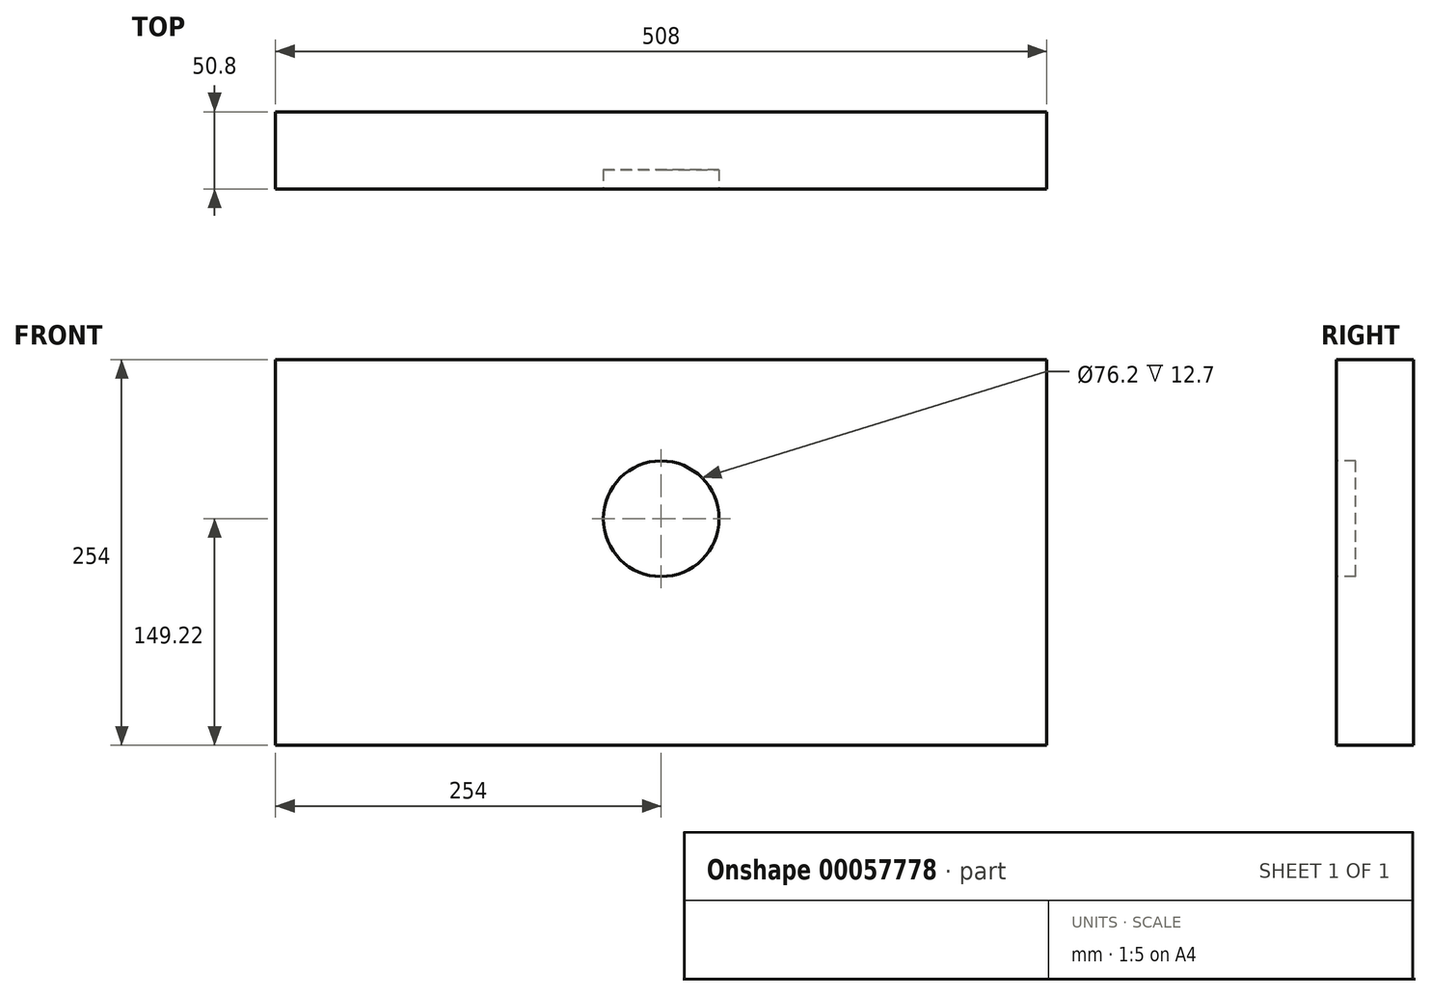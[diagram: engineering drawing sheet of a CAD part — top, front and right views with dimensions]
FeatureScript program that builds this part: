
annotation { "Feature Type Name" : "Feature", "Feature Type Description" : "" }
export const myFeature = defineFeature(function(context is Context, id is Id, definition is map)
    precondition{}
    {
        {
            var Q0;
            Q0=qCreatedBy(makeId("Front.planeOp"),FACE);
            var sketch = newSketch(context, id + "F0", { "sketchPlane" : qUnion([Q0])});
            skLineSegment(sketch, "E0.rect.bottom", {"start": v(254, 127) * mm, "end": v(-254, 127) * mm});
            skLineSegment(sketch, "E0.rect.top", {"start": v(254, -127) * mm, "end": v(-254, -127) * mm});
            skLineSegment(sketch, "E0.rect.left", {"start": v(254, 127) * mm, "end": v(254, -127) * mm});
            skLineSegment(sketch, "E0.rect.right", {"start": v(-254, 127) * mm, "end": v(-254, -127) * mm});
            skSolve(sketch);
        }
        {
            var Q0;
            Q0 = qSketchRegion(id + "F0", true);
            extrude(context, id + "F1", {"entities" : qUnion([Q0]), "depth" : 50.8 * mm});
        }
        {
            var Q0;
            Q0=makeQuery(id+"F1.opExtrude","CAP_FACE",FACE,{"disambiguationData":[OSD([sQuery(id+"F0.wireOp",EDGE,"E0.rect.bottom"),sQuery(id+"F0.wireOp",EDGE,"E0.rect.top"),sQuery(id+"F0.wireOp",EDGE,"E0.rect.left"),sQuery(id+"F0.wireOp",EDGE,"E0.rect.right")])],"isStart":false});
            var sketch = newSketch(context, id + "F2", { "sketchPlane" : qUnion([Q0])});
            skCircle(sketch, "E1", {"center": v(0, 22.22) * mm, "radius": 38.1 * mm});
            skSolve(sketch);
        }
        {
            var Q0;
            Q0 = qSketchRegion(id + "F2", true);
            extrude(context, id + "F3", {"entities" : qUnion([Q0]), "operationType" : NewBodyOperationType.REMOVE, "oppositeDirection" : true, "depth" : 12.7 * mm});
        }
        {
            var Q0;
            Q0=makeQuery(id+"F1.opExtrude","CAP_FACE",FACE,{"disambiguationData":[OSD([sQuery(id+"F0.wireOp",EDGE,"E0.rect.bottom"),sQuery(id+"F0.wireOp",EDGE,"E0.rect.top"),sQuery(id+"F0.wireOp",EDGE,"E0.rect.left"),sQuery(id+"F0.wireOp",EDGE,"E0.rect.right")])],"isStart":false});
            var sketch = newSketch(context, id + "F4", { "sketchPlane" : qUnion([Q0])});
            skCircle(sketch, "E2", {"center": v(-48.27, -19.03) * mm, "radius": 25.4 * mm});
            skSolve(sketch);
        }
        {
            var Q0;
            Q0 = qSketchRegion(id + "F4", true);
            extrude(context, id + "F5", {"entities" : qUnion([Q0]), "operationType" : NewBodyOperationType.ADD, "oppositeDirection" : true, "depth" : 12.7 * mm});
        }
        {
            var Q0;
            Q0=makeQuery(id+"F1.opExtrude","CAP_FACE",FACE,{"disambiguationData":[OSD([sQuery(id+"F0.wireOp",EDGE,"E0.rect.bottom"),sQuery(id+"F0.wireOp",EDGE,"E0.rect.top"),sQuery(id+"F0.wireOp",EDGE,"E0.rect.left"),sQuery(id+"F0.wireOp",EDGE,"E0.rect.right")])],"isStart":false});
            var sketch = newSketch(context, id + "F6", { "sketchPlane" : qUnion([Q0])});
            skCircle(sketch, "E3", {"center": v(-68.17, -34.58) * mm, "radius": 50.63 * mm});
            skSolve(sketch);
        }
        {
            var Q0;
            Q0 = qSketchRegion(id + "F6", true);
            extrude(context, id + "F7", {"entities" : qUnion([Q0]), "operationType" : NewBodyOperationType.ADD, "oppositeDirection" : true, "depth" : 25.4 * mm});
        }
    });
